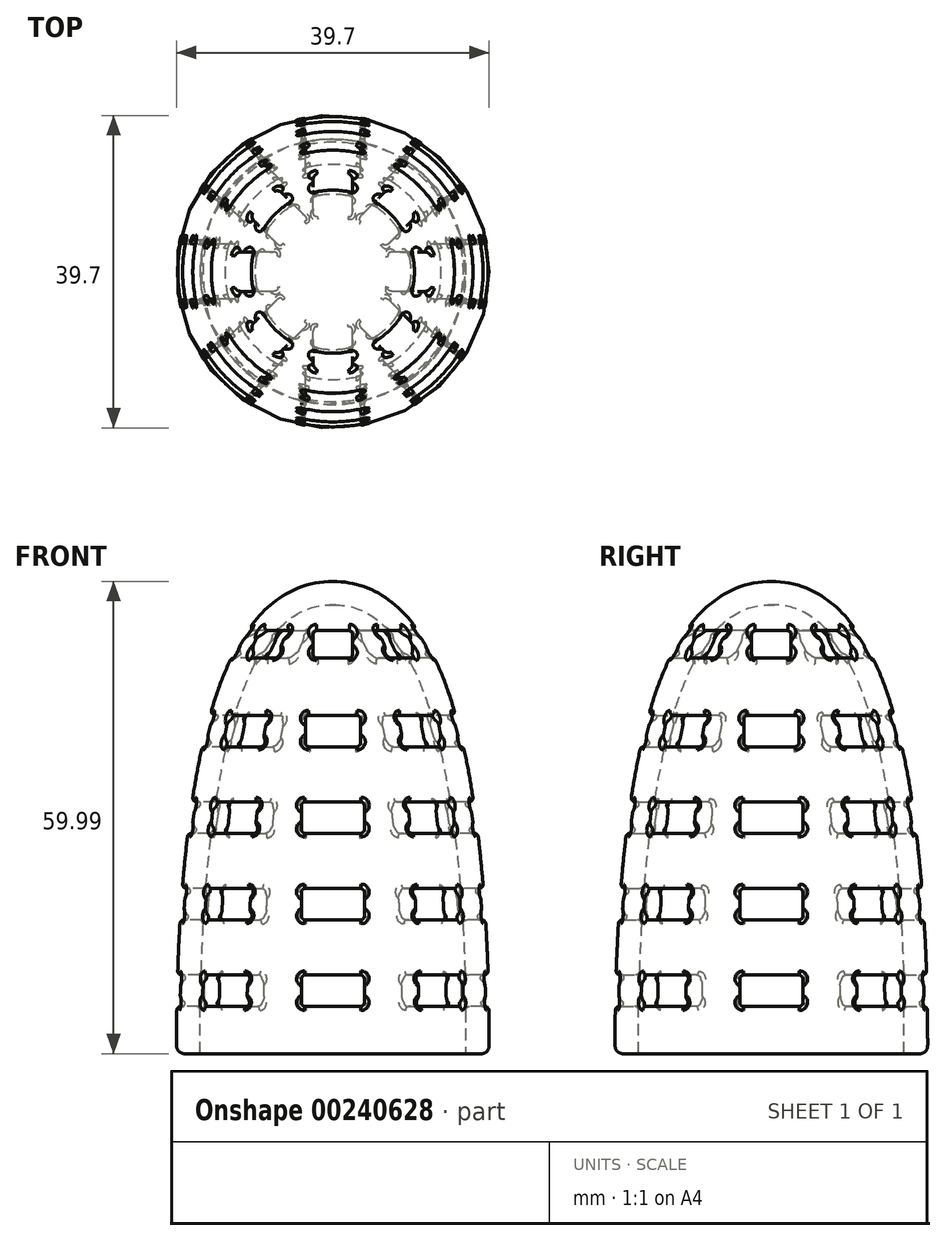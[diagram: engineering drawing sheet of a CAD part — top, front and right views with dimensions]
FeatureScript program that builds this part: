
annotation { "Feature Type Name" : "Feature", "Feature Type Description" : "" }
export const myFeature = defineFeature(function(context is Context, id is Id, definition is map)
    precondition{}
    {
        {
            var Q0;
            Q0=qCreatedBy(makeId("Front.planeOp"),FACE);
            var sketch = newSketch(context, id + "F0", { "sketchPlane" : qUnion([Q0])});
            skFitSpline(sketch, "E0", {"points": [v(0, 60) * mm, v(13.59, 48.77) * mm, v(19.85, 0) * mm], "startDerivative": vector(45.9, 0) * mm, "endDerivative": vector(-0.4, -69.05) * mm});
            skLineSegment(sketch, "E1", {"start": v(19.85, 0) * mm, "end": v(29.85, 0) * mm});
            skFitSpline(sketch, "E2.0", {"points": [v(0, 57) * mm, v(0.73, 57) * mm, v(2.11, 56.84) * mm, v(4.02, 56.13) * mm, v(5.86, 54.92) * mm, v(7.64, 53.14) * mm, v(9.05, 51.12) * mm, v(10.1, 49.2) * mm, v(10.85, 47.59) * mm, v(11.55, 45.81) * mm, v(12.43, 43.25) * mm, v(13.4, 39.7) * mm, v(14.38, 35.02) * mm, v(15.43, 28.37) * mm, v(16.3, 19.58) * mm, v(16.81, 9.16) * mm, v(16.87, 2.86) * mm, v(16.85, 0.02) * mm]});
            skLineSegment(sketch, "E3", {"start": v(16.85, 0.02) * mm, "end": v(11, 0) * mm});
            skLineSegment(sketch, "E4", {"start": v(11, 0) * mm, "end": v(10.99, 4) * mm});
            skLineSegment(sketch, "E5", {"start": v(10.99, 4) * mm, "end": v(16.84, 4.02) * mm});
            skLineSegment(sketch, "E6", {"start": v(16.85, 0.02) * mm, "end": v(19.85, 0) * mm});
            skLineSegment(sketch, "E7", {"start": v(29.85, 0) * mm, "end": v(29.85, 4) * mm});
            skLineSegment(sketch, "E8", {"start": v(29.85, 4) * mm, "end": v(19.84, 4) * mm});
            skLineSegment(sketch, "E9", {"start": v(0, 60) * mm, "end": v(0, 57) * mm});
            skSolve(sketch);
        }
        {
            var Q0;
            Q0=makeQuery(id+"F0.imprint","IMPRINT",FACE,{"disambiguationData":[TD([[makeQuery(id+"F0.imprint","IMPRINT",EDGE,{"derivedFrom":sQuery(id+"F0.wireOp",EDGE,"E0")}),-1.0]])]});
            var Q1;
            Q1=sQuery(id+"F0.wireOp",EDGE,"E9");
            revolve(context, id + "F1", {"entities" : qUnion([Q0]), "axis" : qUnion([Q1]), "revolveType" : RevolveType.FULL});
        }
        {
            var Q0;
            Q0=qCreatedBy(makeId("Front.planeOp"),FACE);
            var sketch = newSketch(context, id + "F2", { "sketchPlane" : qUnion([Q0])});
            skLineSegment(sketch, "E10.bottom", {"start": v(-2.5, 53.75) * mm, "end": v(2.5, 53.75) * mm});
            skLineSegment(sketch, "E10.top", {"start": v(-2.5, 50.25) * mm, "end": v(2.5, 50.25) * mm});
            skLineSegment(sketch, "E10.left", {"start": v(-2.5, 53.75) * mm, "end": v(-2.5, 50.25) * mm});
            skLineSegment(sketch, "E10.right", {"start": v(2.5, 53.75) * mm, "end": v(2.5, 50.25) * mm});
            skPoint(sketch, "E10.middle", {"position": v(0, 52) * mm});
            skLineSegment(sketch, "E11.bottom", {"start": v(-3.5, 43) * mm, "end": v(3.5, 43) * mm});
            skLineSegment(sketch, "E11.top", {"start": v(-3.5, 39) * mm, "end": v(3.5, 39) * mm});
            skLineSegment(sketch, "E11.left", {"start": v(-3.5, 43) * mm, "end": v(-3.5, 39) * mm});
            skLineSegment(sketch, "E11.right", {"start": v(3.5, 43) * mm, "end": v(3.5, 39) * mm});
            skPoint(sketch, "E11.middle", {"position": v(0, 41) * mm});
            skLineSegment(sketch, "E12.bottom", {"start": v(-4, 32) * mm, "end": v(4, 32) * mm});
            skLineSegment(sketch, "E12.top", {"start": v(-4, 28) * mm, "end": v(4, 28) * mm});
            skLineSegment(sketch, "E12.left", {"start": v(-4, 32) * mm, "end": v(-4, 28) * mm});
            skLineSegment(sketch, "E12.right", {"start": v(4, 32) * mm, "end": v(4, 28) * mm});
            skPoint(sketch, "E12.middle", {"position": v(0, 30) * mm});
            skLineSegment(sketch, "E13.bottom", {"start": v(-4, 21) * mm, "end": v(4, 21) * mm});
            skLineSegment(sketch, "E13.top", {"start": v(-4, 17) * mm, "end": v(4, 17) * mm});
            skLineSegment(sketch, "E13.left", {"start": v(-4, 21) * mm, "end": v(-4, 17) * mm});
            skLineSegment(sketch, "E13.right", {"start": v(4, 21) * mm, "end": v(4, 17) * mm});
            skPoint(sketch, "E13.middle", {"position": v(0, 19) * mm});
            skLineSegment(sketch, "E14.bottom", {"start": v(-4, 10) * mm, "end": v(4, 10) * mm});
            skLineSegment(sketch, "E14.top", {"start": v(-4, 6) * mm, "end": v(4, 6) * mm});
            skLineSegment(sketch, "E14.left", {"start": v(-4, 10) * mm, "end": v(-4, 6) * mm});
            skLineSegment(sketch, "E14.right", {"start": v(4, 10) * mm, "end": v(4, 6) * mm});
            skPoint(sketch, "E14.middle", {"position": v(0, 8) * mm});
            skSolve(sketch);
        }
        {
            var Q0;
            Q0 = qSketchRegion(id + "F2", true);
            extrude(context, id + "F3", {"entities" : qUnion([Q0]), "operationType" : NewBodyOperationType.REMOVE, "endBound" : BoundingType.SYMMETRIC, "depth" : 50 * mm});
        }
        {
            var Q0;
            Q0=makeQuery(id+"F3.boolean.opBoolean","COPY",EDGE,{"disambiguationData":[OD(0.0)],"derivedFrom":makeQuery(id+"F3.opExtrude","SWEPT_EDGE",EDGE,{"disambiguationData":[OSD([sQuery(id+"F2.wireOp",EDGE,"E11.top"),sQuery(id+"F2.wireOp",EDGE,"E11.left")])]})});
            var Q1;
            Q1=makeQuery(id+"F3.boolean.opBoolean","COPY",EDGE,{"disambiguationData":[OD(0.0)],"derivedFrom":makeQuery(id+"F3.opExtrude","SWEPT_EDGE",EDGE,{"disambiguationData":[OSD([sQuery(id+"F2.wireOp",EDGE,"E11.top"),sQuery(id+"F2.wireOp",EDGE,"E11.right")])]})});
            var Q2;
            Q2=makeQuery(id+"F3.boolean.opBoolean","COPY",EDGE,{"disambiguationData":[OD(0.0)],"derivedFrom":makeQuery(id+"F3.opExtrude","SWEPT_EDGE",EDGE,{"disambiguationData":[OSD([sQuery(id+"F2.wireOp",EDGE,"E11.bottom"),sQuery(id+"F2.wireOp",EDGE,"E11.left")])]})});
            var Q3;
            Q3=makeQuery(id+"F3.boolean.opBoolean","COPY",EDGE,{"disambiguationData":[OD(0.0)],"derivedFrom":makeQuery(id+"F3.opExtrude","SWEPT_EDGE",EDGE,{"disambiguationData":[OSD([sQuery(id+"F2.wireOp",EDGE,"E10.bottom"),sQuery(id+"F2.wireOp",EDGE,"E10.left")])]})});
            var Q4;
            Q4=makeQuery(id+"F3.boolean.opBoolean","COPY",EDGE,{"disambiguationData":[OD(1.0)],"derivedFrom":makeQuery(id+"F3.opExtrude","SWEPT_EDGE",EDGE,{"disambiguationData":[OSD([sQuery(id+"F2.wireOp",EDGE,"E11.bottom"),sQuery(id+"F2.wireOp",EDGE,"E11.right")])]})});
            var Q5;
            Q5=makeQuery(id+"F3.boolean.opBoolean","COPY",EDGE,{"disambiguationData":[OD(1.0)],"derivedFrom":makeQuery(id+"F3.opExtrude","SWEPT_EDGE",EDGE,{"disambiguationData":[OSD([sQuery(id+"F2.wireOp",EDGE,"E10.bottom"),sQuery(id+"F2.wireOp",EDGE,"E10.right")])]})});
            var Q6;
            Q6=makeQuery(id+"F3.boolean.opBoolean","COPY",EDGE,{"disambiguationData":[OD(0.0)],"derivedFrom":makeQuery(id+"F3.opExtrude","SWEPT_EDGE",EDGE,{"disambiguationData":[OSD([sQuery(id+"F2.wireOp",EDGE,"E10.bottom"),sQuery(id+"F2.wireOp",EDGE,"E10.right")])]})});
            var Q7;
            Q7=makeQuery(id+"F3.boolean.opBoolean","COPY",EDGE,{"disambiguationData":[OD(0.0)],"derivedFrom":makeQuery(id+"F3.opExtrude","SWEPT_EDGE",EDGE,{"disambiguationData":[OSD([sQuery(id+"F2.wireOp",EDGE,"E11.bottom"),sQuery(id+"F2.wireOp",EDGE,"E11.right")])]})});
            var Q8;
            Q8=makeQuery(id+"F3.boolean.opBoolean","COPY",EDGE,{"disambiguationData":[OD(0.0)],"derivedFrom":makeQuery(id+"F3.opExtrude","SWEPT_EDGE",EDGE,{"disambiguationData":[OSD([sQuery(id+"F2.wireOp",EDGE,"E13.top"),sQuery(id+"F2.wireOp",EDGE,"E13.left")])]})});
            var Q9;
            Q9=makeQuery(id+"F3.boolean.opBoolean","COPY",EDGE,{"disambiguationData":[OD(0.0)],"derivedFrom":makeQuery(id+"F3.opExtrude","SWEPT_EDGE",EDGE,{"disambiguationData":[OSD([sQuery(id+"F2.wireOp",EDGE,"E14.top"),sQuery(id+"F2.wireOp",EDGE,"E14.left")])]})});
            var Q10;
            Q10=makeQuery(id+"F3.boolean.opBoolean","COPY",FACE,{"disambiguationData":[OD(0.0)],"derivedFrom":makeQuery(id+"F3.opExtrude","SWEPT_FACE",FACE,{"disambiguationData":[OSD([sQuery(id+"F2.wireOp",EDGE,"E14.top")])]})});
            var Q11;
            Q11=makeQuery(id+"F3.boolean.opBoolean","COPY",FACE,{"disambiguationData":[OD(0.0)],"derivedFrom":makeQuery(id+"F3.opExtrude","SWEPT_FACE",FACE,{"disambiguationData":[OSD([sQuery(id+"F2.wireOp",EDGE,"E14.bottom")])]})});
            var Q12;
            Q12=makeQuery(id+"F3.boolean.opBoolean","COPY",FACE,{"disambiguationData":[OD(0.0)],"derivedFrom":makeQuery(id+"F3.opExtrude","SWEPT_FACE",FACE,{"disambiguationData":[OSD([sQuery(id+"F2.wireOp",EDGE,"E13.bottom")])]})});
            var Q13;
            Q13=makeQuery(id+"F3.boolean.opBoolean","COPY",FACE,{"disambiguationData":[OD(0.0)],"derivedFrom":makeQuery(id+"F3.opExtrude","SWEPT_FACE",FACE,{"disambiguationData":[OSD([sQuery(id+"F2.wireOp",EDGE,"E12.top")])]})});
            var Q14;
            Q14=makeQuery(id+"F3.boolean.opBoolean","COPY",FACE,{"disambiguationData":[OD(0.0)],"derivedFrom":makeQuery(id+"F3.opExtrude","SWEPT_FACE",FACE,{"disambiguationData":[OSD([sQuery(id+"F2.wireOp",EDGE,"E13.top")])]})});
            var Q15;
            Q15=makeQuery(id+"F3.boolean.opBoolean","INTERSECT",EDGE,{"disambiguationData":[OD(0.0)],"derivedFrom":[makeQuery(id+"F1.opRevolve","SWEPT_FACE",FACE,{"disambiguationData":[OSD([sQuery(id+"F0.wireOp",EDGE,"E0")])]}),makeQuery(id+"F3.opExtrude","SWEPT_FACE",FACE,{"disambiguationData":[OSD([sQuery(id+"F2.wireOp",EDGE,"E12.bottom")])]})]});
            var Q16;
            Q16=makeQuery(id+"F3.boolean.opBoolean","COPY",FACE,{"disambiguationData":[OD(0.0)],"derivedFrom":makeQuery(id+"F3.opExtrude","SWEPT_FACE",FACE,{"disambiguationData":[OSD([sQuery(id+"F2.wireOp",EDGE,"E12.bottom")])]})});
            var Q17;
            Q17=makeQuery(id+"F3.boolean.opBoolean","COPY",FACE,{"disambiguationData":[OD(0.0)],"derivedFrom":makeQuery(id+"F3.opExtrude","SWEPT_FACE",FACE,{"disambiguationData":[OSD([sQuery(id+"F2.wireOp",EDGE,"E11.bottom")])]})});
            var Q18;
            Q18=makeQuery(id+"F3.boolean.opBoolean","COPY",FACE,{"disambiguationData":[OD(0.0)],"derivedFrom":makeQuery(id+"F3.opExtrude","SWEPT_FACE",FACE,{"disambiguationData":[OSD([sQuery(id+"F2.wireOp",EDGE,"E11.top")])]})});
            var Q19;
            Q19=makeQuery(id+"F3.boolean.opBoolean","COPY",FACE,{"disambiguationData":[OD(0.0)],"derivedFrom":makeQuery(id+"F3.opExtrude","SWEPT_FACE",FACE,{"disambiguationData":[OSD([sQuery(id+"F2.wireOp",EDGE,"E10.top")])]})});
            var Q20;
            Q20=makeQuery(id+"F3.boolean.opBoolean","COPY",FACE,{"disambiguationData":[OD(0.0)],"derivedFrom":makeQuery(id+"F3.opExtrude","SWEPT_FACE",FACE,{"disambiguationData":[OSD([sQuery(id+"F2.wireOp",EDGE,"E10.bottom")])]})});
            var Q21;
            Q21=makeQuery(id+"F3.boolean.opBoolean","COPY",FACE,{"disambiguationData":[OD(1.0)],"derivedFrom":makeQuery(id+"F3.opExtrude","SWEPT_FACE",FACE,{"disambiguationData":[OSD([sQuery(id+"F2.wireOp",EDGE,"E11.bottom")])]})});
            var Q22;
            Q22=makeQuery(id+"F3.boolean.opBoolean","COPY",FACE,{"disambiguationData":[OD(1.0)],"derivedFrom":makeQuery(id+"F3.opExtrude","SWEPT_FACE",FACE,{"disambiguationData":[OSD([sQuery(id+"F2.wireOp",EDGE,"E12.bottom")])]})});
            var Q23;
            Q23=makeQuery(id+"F3.boolean.opBoolean","COPY",FACE,{"disambiguationData":[OD(1.0)],"derivedFrom":makeQuery(id+"F3.opExtrude","SWEPT_FACE",FACE,{"disambiguationData":[OSD([sQuery(id+"F2.wireOp",EDGE,"E13.bottom")])]})});
            var Q24;
            Q24=makeQuery(id+"F3.boolean.opBoolean","COPY",FACE,{"disambiguationData":[OD(1.0)],"derivedFrom":makeQuery(id+"F3.opExtrude","SWEPT_FACE",FACE,{"disambiguationData":[OSD([sQuery(id+"F2.wireOp",EDGE,"E10.bottom")])]})});
            var Q25;
            Q25=makeQuery(id+"F3.boolean.opBoolean","COPY",FACE,{"disambiguationData":[OD(1.0)],"derivedFrom":makeQuery(id+"F3.opExtrude","SWEPT_FACE",FACE,{"disambiguationData":[OSD([sQuery(id+"F2.wireOp",EDGE,"E14.top")])]})});
            var Q26;
            Q26=makeQuery(id+"F3.boolean.opBoolean","COPY",FACE,{"disambiguationData":[OD(1.0)],"derivedFrom":makeQuery(id+"F3.opExtrude","SWEPT_FACE",FACE,{"disambiguationData":[OSD([sQuery(id+"F2.wireOp",EDGE,"E13.top")])]})});
            var Q27;
            Q27=makeQuery(id+"F3.boolean.opBoolean","COPY",FACE,{"disambiguationData":[OD(1.0)],"derivedFrom":makeQuery(id+"F3.opExtrude","SWEPT_FACE",FACE,{"disambiguationData":[OSD([sQuery(id+"F2.wireOp",EDGE,"E12.top")])]})});
            var Q28;
            Q28=makeQuery(id+"F3.boolean.opBoolean","COPY",FACE,{"disambiguationData":[OD(1.0)],"derivedFrom":makeQuery(id+"F3.opExtrude","SWEPT_FACE",FACE,{"disambiguationData":[OSD([sQuery(id+"F2.wireOp",EDGE,"E11.top")])]})});
            var Q29;
            Q29=makeQuery(id+"F3.boolean.opBoolean","COPY",FACE,{"disambiguationData":[OD(1.0)],"derivedFrom":makeQuery(id+"F3.opExtrude","SWEPT_FACE",FACE,{"disambiguationData":[OSD([sQuery(id+"F2.wireOp",EDGE,"E10.top")])]})});
            var Q30;
            Q30=makeQuery(id+"F3.boolean.opBoolean","COPY",FACE,{"disambiguationData":[OD(1.0)],"derivedFrom":makeQuery(id+"F3.opExtrude","SWEPT_FACE",FACE,{"disambiguationData":[OSD([sQuery(id+"F2.wireOp",EDGE,"E14.bottom")])]})});
            fillet(context, id + "F4", {"entities" : qUnion([Q0, Q1, Q2, Q3, Q4, Q5, Q6, Q7, Q8, Q9, Q10, Q11, Q12, Q13, Q14, Q15, Q16, Q17, Q18, Q19, Q20, Q21, Q22, Q23, Q24, Q25, Q26, Q27, Q28, Q29, Q30]), "radius" : .5 * mm, "tangentPropagation" : true, "allowEdgeOverflow" : false});
        }
        {
            var Q0;
            Q0=qCreatedBy(makeId("Right.planeOp"),FACE);
            var sketch = newSketch(context, id + "F5", { "sketchPlane" : qUnion([Q0])});
            skLineSegment(sketch, "E15.bottom", {"start": v(2.5, 53.75) * mm, "end": v(-2.5, 53.75) * mm});
            skLineSegment(sketch, "E15.top", {"start": v(2.5, 50.25) * mm, "end": v(-2.5, 50.25) * mm});
            skLineSegment(sketch, "E15.left", {"start": v(2.5, 53.75) * mm, "end": v(2.5, 50.25) * mm});
            skLineSegment(sketch, "E15.right", {"start": v(-2.5, 53.75) * mm, "end": v(-2.5, 50.25) * mm});
            skPoint(sketch, "E15.middle", {"position": v(0, 52) * mm});
            skLineSegment(sketch, "E16.bottom", {"start": v(3.5, 43) * mm, "end": v(-3.5, 43) * mm});
            skLineSegment(sketch, "E16.top", {"start": v(3.5, 39) * mm, "end": v(-3.5, 39) * mm});
            skLineSegment(sketch, "E16.left", {"start": v(3.5, 43) * mm, "end": v(3.5, 39) * mm});
            skLineSegment(sketch, "E16.right", {"start": v(-3.5, 43) * mm, "end": v(-3.5, 39) * mm});
            skPoint(sketch, "E16.middle", {"position": v(0, 41) * mm});
            skLineSegment(sketch, "E17.bottom", {"start": v(4, 32) * mm, "end": v(-4, 32) * mm});
            skLineSegment(sketch, "E17.top", {"start": v(4, 28) * mm, "end": v(-4, 28) * mm});
            skLineSegment(sketch, "E17.left", {"start": v(4, 32) * mm, "end": v(4, 28) * mm});
            skLineSegment(sketch, "E17.right", {"start": v(-4, 32) * mm, "end": v(-4, 28) * mm});
            skPoint(sketch, "E17.middle", {"position": v(0, 30) * mm});
            skLineSegment(sketch, "E18.bottom", {"start": v(4, 21) * mm, "end": v(-4, 21) * mm});
            skLineSegment(sketch, "E18.top", {"start": v(4, 17) * mm, "end": v(-4, 17) * mm});
            skLineSegment(sketch, "E18.left", {"start": v(4, 21) * mm, "end": v(4, 17) * mm});
            skLineSegment(sketch, "E18.right", {"start": v(-4, 21) * mm, "end": v(-4, 17) * mm});
            skPoint(sketch, "E18.middle", {"position": v(0, 19) * mm});
            skLineSegment(sketch, "E19.bottom", {"start": v(4, 10) * mm, "end": v(-4, 10) * mm});
            skLineSegment(sketch, "E19.top", {"start": v(4, 6) * mm, "end": v(-4, 6) * mm});
            skLineSegment(sketch, "E19.left", {"start": v(4, 10) * mm, "end": v(4, 6) * mm});
            skLineSegment(sketch, "E19.right", {"start": v(-4, 10) * mm, "end": v(-4, 6) * mm});
            skPoint(sketch, "E19.middle", {"position": v(0, 8) * mm});
            skSolve(sketch);
        }
        {
            var Q0;
            Q0 = qSketchRegion(id + "F5", true);
            extrude(context, id + "F6", {"entities" : qUnion([Q0]), "operationType" : NewBodyOperationType.REMOVE, "endBound" : BoundingType.SYMMETRIC, "depth" : 50 * mm});
        }
        {
            var Q0;
            Q0=qCreatedBy(makeId("Front.planeOp"),FACE);
            var Q1;
            Q1=sQuery(id+"F0.wireOp",EDGE,"E7");
            cPlane(context, id + "F7", {"entities" : qUnion([Q0, Q1]), "cplaneType" : CPlaneType.LINE_ANGLE, "offset" : 25 * mm, "angle" : 45 * degree, "width" : 150 * mm, "height" : 150 * mm});
        }
        {
            var Q0;
            Q0=qCreatedBy(id+"F7.planeOp",FACE);
            var sketch = newSketch(context, id + "F8", { "sketchPlane" : qUnion([Q0])});
            skLineSegment(sketch, "E20.bottom", {"start": v(3.5, 43) * mm, "end": v(-3.5, 43) * mm});
            skLineSegment(sketch, "E20.top", {"start": v(3.5, 39) * mm, "end": v(-3.5, 39) * mm});
            skLineSegment(sketch, "E20.left", {"start": v(3.5, 43) * mm, "end": v(3.5, 39) * mm});
            skLineSegment(sketch, "E20.right", {"start": v(-3.5, 43) * mm, "end": v(-3.5, 39) * mm});
            skPoint(sketch, "E20.middle", {"position": v(0, 41) * mm});
            skLineSegment(sketch, "E21.bottom", {"start": v(4, 32) * mm, "end": v(-4, 32) * mm});
            skLineSegment(sketch, "E21.top", {"start": v(4, 28) * mm, "end": v(-4, 28) * mm});
            skLineSegment(sketch, "E21.left", {"start": v(4, 32) * mm, "end": v(4, 28) * mm});
            skLineSegment(sketch, "E21.right", {"start": v(-4, 32) * mm, "end": v(-4, 28) * mm});
            skPoint(sketch, "E21.middle", {"position": v(0, 30) * mm});
            skLineSegment(sketch, "E22.bottom", {"start": v(4, 21) * mm, "end": v(-4, 21) * mm});
            skLineSegment(sketch, "E22.top", {"start": v(4, 17) * mm, "end": v(-4, 17) * mm});
            skLineSegment(sketch, "E22.left", {"start": v(4, 21) * mm, "end": v(4, 17) * mm});
            skLineSegment(sketch, "E22.right", {"start": v(-4, 21) * mm, "end": v(-4, 17) * mm});
            skPoint(sketch, "E22.middle", {"position": v(0, 19) * mm});
            skLineSegment(sketch, "E23.bottom", {"start": v(4, 10) * mm, "end": v(-4, 10) * mm});
            skLineSegment(sketch, "E23.top", {"start": v(4, 6) * mm, "end": v(-4, 6) * mm});
            skLineSegment(sketch, "E23.left", {"start": v(4, 10) * mm, "end": v(4, 6) * mm});
            skLineSegment(sketch, "E23.right", {"start": v(-4, 10) * mm, "end": v(-4, 6) * mm});
            skPoint(sketch, "E23.middle", {"position": v(0, 8) * mm});
            skLineSegment(sketch, "E24.bottom", {"start": v(2.5, 53.75) * mm, "end": v(-2.5, 53.75) * mm});
            skLineSegment(sketch, "E24.top", {"start": v(2.5, 50.25) * mm, "end": v(-2.5, 50.25) * mm});
            skLineSegment(sketch, "E24.left", {"start": v(2.5, 53.75) * mm, "end": v(2.5, 50.25) * mm});
            skLineSegment(sketch, "E24.right", {"start": v(-2.5, 53.75) * mm, "end": v(-2.5, 50.25) * mm});
            skPoint(sketch, "E24.middle", {"position": v(0, 52) * mm});
            skSolve(sketch);
        }
        {
            var Q0;
            Q0 = qSketchRegion(id + "F8", true);
            extrude(context, id + "F9", {"entities" : qUnion([Q0]), "operationType" : NewBodyOperationType.REMOVE, "depth" : 50 * mm});
        }
        {
            var Q0;
            Q0=qCreatedBy(makeId("Right.planeOp"),FACE);
            var Q1;
            Q1=sQuery(id+"F0.wireOp",EDGE,"E7");
            cPlane(context, id + "F10", {"entities" : qUnion([Q0, Q1]), "cplaneType" : CPlaneType.LINE_ANGLE, "offset" : 25 * mm, "angle" : 45 * degree, "width" : 150 * mm, "height" : 150 * mm});
        }
        {
            var Q0;
            Q0=qCreatedBy(id+"F10.planeOp",FACE);
            var sketch = newSketch(context, id + "F11", { "sketchPlane" : qUnion([Q0])});
            skLineSegment(sketch, "E25.bottom", {"start": v(-2.5, 53.75) * mm, "end": v(2.5, 53.75) * mm});
            skLineSegment(sketch, "E25.top", {"start": v(-2.5, 50.25) * mm, "end": v(2.5, 50.25) * mm});
            skLineSegment(sketch, "E25.left", {"start": v(-2.5, 53.75) * mm, "end": v(-2.5, 50.25) * mm});
            skLineSegment(sketch, "E25.right", {"start": v(2.5, 53.75) * mm, "end": v(2.5, 50.25) * mm});
            skPoint(sketch, "E25.middle", {"position": v(0, 52) * mm});
            skLineSegment(sketch, "E26.bottom", {"start": v(-3.5, 43) * mm, "end": v(3.5, 43) * mm});
            skLineSegment(sketch, "E26.top", {"start": v(-3.5, 39) * mm, "end": v(3.5, 39) * mm});
            skLineSegment(sketch, "E26.left", {"start": v(-3.5, 43) * mm, "end": v(-3.5, 39) * mm});
            skLineSegment(sketch, "E26.right", {"start": v(3.5, 43) * mm, "end": v(3.5, 39) * mm});
            skPoint(sketch, "E26.middle", {"position": v(0, 41) * mm});
            skLineSegment(sketch, "E27.bottom", {"start": v(-4, 32) * mm, "end": v(4, 32) * mm});
            skLineSegment(sketch, "E27.top", {"start": v(-4, 28) * mm, "end": v(4, 28) * mm});
            skLineSegment(sketch, "E27.left", {"start": v(-4, 32) * mm, "end": v(-4, 28) * mm});
            skLineSegment(sketch, "E27.right", {"start": v(4, 32) * mm, "end": v(4, 28) * mm});
            skPoint(sketch, "E27.middle", {"position": v(0, 30) * mm});
            skLineSegment(sketch, "E28.bottom", {"start": v(-4, 21) * mm, "end": v(4, 21) * mm});
            skLineSegment(sketch, "E28.top", {"start": v(-4, 17) * mm, "end": v(4, 17) * mm});
            skLineSegment(sketch, "E28.left", {"start": v(-4, 21) * mm, "end": v(-4, 17) * mm});
            skLineSegment(sketch, "E28.right", {"start": v(4, 21) * mm, "end": v(4, 17) * mm});
            skPoint(sketch, "E28.middle", {"position": v(0, 19) * mm});
            skLineSegment(sketch, "E29.bottom", {"start": v(-4, 10) * mm, "end": v(4, 10) * mm});
            skLineSegment(sketch, "E29.top", {"start": v(-4, 6) * mm, "end": v(4, 6) * mm});
            skLineSegment(sketch, "E29.left", {"start": v(-4, 10) * mm, "end": v(-4, 6) * mm});
            skLineSegment(sketch, "E29.right", {"start": v(4, 10) * mm, "end": v(4, 6) * mm});
            skPoint(sketch, "E29.middle", {"position": v(0, 8) * mm});
            skSolve(sketch);
        }
        {
            var Q0;
            Q0 = qSketchRegion(id + "F11", true);
            extrude(context, id + "F12", {"entities" : qUnion([Q0]), "operationType" : NewBodyOperationType.REMOVE, "depth" : 50 * mm});
        }
        {
            var Q0;
            Q0=makeQuery(id+"F9.boolean.opBoolean","COPY",FACE,{"disambiguationData":[OD(0.0)],"derivedFrom":makeQuery(id+"F9.opExtrude","SWEPT_FACE",FACE,{"disambiguationData":[OSD([sQuery(id+"F8.wireOp",EDGE,"E20.bottom")])]})});
            var Q1;
            Q1=makeQuery(id+"F9.boolean.opBoolean","COPY",FACE,{"disambiguationData":[OD(0.0)],"derivedFrom":makeQuery(id+"F9.opExtrude","SWEPT_FACE",FACE,{"disambiguationData":[OSD([sQuery(id+"F8.wireOp",EDGE,"E21.bottom")])]})});
            var Q2;
            Q2=makeQuery(id+"F6.boolean.opBoolean","COPY",FACE,{"disambiguationData":[OD(0.0)],"derivedFrom":makeQuery(id+"F6.opExtrude","SWEPT_FACE",FACE,{"disambiguationData":[OSD([sQuery(id+"F5.wireOp",EDGE,"E16.bottom")])]})});
            var Q3;
            Q3=makeQuery(id+"F6.boolean.opBoolean","COPY",FACE,{"disambiguationData":[OD(0.0)],"derivedFrom":makeQuery(id+"F6.opExtrude","SWEPT_FACE",FACE,{"disambiguationData":[OSD([sQuery(id+"F5.wireOp",EDGE,"E17.bottom")])]})});
            var Q4;
            Q4=makeQuery(id+"F6.boolean.opBoolean","COPY",FACE,{"disambiguationData":[OD(0.0)],"derivedFrom":makeQuery(id+"F6.opExtrude","SWEPT_FACE",FACE,{"disambiguationData":[OSD([sQuery(id+"F5.wireOp",EDGE,"E18.bottom")])]})});
            var Q5;
            Q5=makeQuery(id+"F9.boolean.opBoolean","COPY",FACE,{"disambiguationData":[OD(0.0)],"derivedFrom":makeQuery(id+"F9.opExtrude","SWEPT_FACE",FACE,{"disambiguationData":[OSD([sQuery(id+"F8.wireOp",EDGE,"E22.bottom")])]})});
            var Q6;
            Q6=makeQuery(id+"F6.boolean.opBoolean","COPY",FACE,{"disambiguationData":[OD(0.0)],"derivedFrom":makeQuery(id+"F6.opExtrude","SWEPT_FACE",FACE,{"disambiguationData":[OSD([sQuery(id+"F5.wireOp",EDGE,"E15.bottom")])]})});
            var Q7;
            Q7=makeQuery(id+"F9.boolean.opBoolean","COPY",FACE,{"disambiguationData":[OD(0.0)],"derivedFrom":makeQuery(id+"F9.opExtrude","SWEPT_FACE",FACE,{"disambiguationData":[OSD([sQuery(id+"F8.wireOp",EDGE,"E24.bottom")])]})});
            var Q8;
            Q8=makeQuery(id+"F12.boolean.opBoolean","COPY",FACE,{"disambiguationData":[OD(0.0)],"derivedFrom":makeQuery(id+"F12.opExtrude","SWEPT_FACE",FACE,{"disambiguationData":[OSD([sQuery(id+"F11.wireOp",EDGE,"E26.bottom")])]})});
            var Q9;
            Q9=makeQuery(id+"F12.boolean.opBoolean","INTERSECT",EDGE,{"disambiguationData":[OD(0.0)],"derivedFrom":[makeQuery(id+"F1.opRevolve","SWEPT_FACE",FACE,{"disambiguationData":[OSD([sQuery(id+"F0.wireOp",EDGE,"E0")])]}),makeQuery(id+"F12.opExtrude","SWEPT_FACE",FACE,{"disambiguationData":[OSD([sQuery(id+"F11.wireOp",EDGE,"E27.bottom")])]})]});
            var Q10;
            Q10=makeQuery(id+"F12.boolean.opBoolean","COPY",FACE,{"disambiguationData":[OD(0.0)],"derivedFrom":makeQuery(id+"F12.opExtrude","SWEPT_FACE",FACE,{"disambiguationData":[OSD([sQuery(id+"F11.wireOp",EDGE,"E27.bottom")])]})});
            var Q11;
            Q11=makeQuery(id+"F12.boolean.opBoolean","COPY",FACE,{"disambiguationData":[OD(0.0)],"derivedFrom":makeQuery(id+"F12.opExtrude","SWEPT_FACE",FACE,{"disambiguationData":[OSD([sQuery(id+"F11.wireOp",EDGE,"E28.bottom")])]})});
            var Q12;
            Q12=makeQuery(id+"F6.boolean.opBoolean","COPY",FACE,{"disambiguationData":[OD(0.0)],"derivedFrom":makeQuery(id+"F6.opExtrude","SWEPT_FACE",FACE,{"disambiguationData":[OSD([sQuery(id+"F5.wireOp",EDGE,"E19.top")])]})});
            var Q13;
            Q13=makeQuery(id+"F9.boolean.opBoolean","COPY",FACE,{"disambiguationData":[OD(0.0)],"derivedFrom":makeQuery(id+"F9.opExtrude","SWEPT_FACE",FACE,{"disambiguationData":[OSD([sQuery(id+"F8.wireOp",EDGE,"E23.top")])]})});
            var Q14;
            Q14=makeQuery(id+"F9.boolean.opBoolean","COPY",FACE,{"disambiguationData":[OD(0.0)],"derivedFrom":makeQuery(id+"F9.opExtrude","SWEPT_FACE",FACE,{"disambiguationData":[OSD([sQuery(id+"F8.wireOp",EDGE,"E22.top")])]})});
            var Q15;
            Q15=makeQuery(id+"F9.boolean.opBoolean","COPY",FACE,{"disambiguationData":[OD(0.0)],"derivedFrom":makeQuery(id+"F9.opExtrude","SWEPT_FACE",FACE,{"disambiguationData":[OSD([sQuery(id+"F8.wireOp",EDGE,"E21.top")])]})});
            var Q16;
            Q16=makeQuery(id+"F9.boolean.opBoolean","COPY",FACE,{"disambiguationData":[OD(0.0)],"derivedFrom":makeQuery(id+"F9.opExtrude","SWEPT_FACE",FACE,{"disambiguationData":[OSD([sQuery(id+"F8.wireOp",EDGE,"E20.top")])]})});
            var Q17;
            Q17=makeQuery(id+"F6.boolean.opBoolean","COPY",FACE,{"disambiguationData":[OD(0.0)],"derivedFrom":makeQuery(id+"F6.opExtrude","SWEPT_FACE",FACE,{"disambiguationData":[OSD([sQuery(id+"F5.wireOp",EDGE,"E17.top")])]})});
            var Q18;
            Q18=makeQuery(id+"F6.boolean.opBoolean","COPY",FACE,{"disambiguationData":[OD(0.0)],"derivedFrom":makeQuery(id+"F6.opExtrude","SWEPT_FACE",FACE,{"disambiguationData":[OSD([sQuery(id+"F5.wireOp",EDGE,"E16.top")])]})});
            var Q19;
            Q19=makeQuery(id+"F6.boolean.opBoolean","COPY",FACE,{"disambiguationData":[OD(0.0)],"derivedFrom":makeQuery(id+"F6.opExtrude","SWEPT_FACE",FACE,{"disambiguationData":[OSD([sQuery(id+"F5.wireOp",EDGE,"E15.top")])]})});
            var Q20;
            Q20=makeQuery(id+"F9.boolean.opBoolean","COPY",FACE,{"disambiguationData":[OD(0.0)],"derivedFrom":makeQuery(id+"F9.opExtrude","SWEPT_FACE",FACE,{"disambiguationData":[OSD([sQuery(id+"F8.wireOp",EDGE,"E24.top")])]})});
            var Q21;
            Q21=makeQuery(id+"F12.boolean.opBoolean","COPY",FACE,{"disambiguationData":[OD(0.0)],"derivedFrom":makeQuery(id+"F12.opExtrude","SWEPT_FACE",FACE,{"disambiguationData":[OSD([sQuery(id+"F11.wireOp",EDGE,"E25.top")])]})});
            var Q22;
            Q22=makeQuery(id+"F12.boolean.opBoolean","COPY",FACE,{"disambiguationData":[OD(0.0)],"derivedFrom":makeQuery(id+"F12.opExtrude","SWEPT_FACE",FACE,{"disambiguationData":[OSD([sQuery(id+"F11.wireOp",EDGE,"E26.top")])]})});
            var Q23;
            Q23=makeQuery(id+"F12.boolean.opBoolean","COPY",FACE,{"disambiguationData":[OD(0.0)],"derivedFrom":makeQuery(id+"F12.opExtrude","SWEPT_FACE",FACE,{"disambiguationData":[OSD([sQuery(id+"F11.wireOp",EDGE,"E27.top")])]})});
            var Q24;
            Q24=makeQuery(id+"F12.boolean.opBoolean","COPY",FACE,{"disambiguationData":[OD(0.0)],"derivedFrom":makeQuery(id+"F12.opExtrude","SWEPT_FACE",FACE,{"disambiguationData":[OSD([sQuery(id+"F11.wireOp",EDGE,"E28.top")])]})});
            var Q25;
            Q25=makeQuery(id+"F12.boolean.opBoolean","COPY",FACE,{"disambiguationData":[OD(0.0)],"derivedFrom":makeQuery(id+"F12.opExtrude","SWEPT_FACE",FACE,{"disambiguationData":[OSD([sQuery(id+"F11.wireOp",EDGE,"E29.top")])]})});
            var Q26;
            Q26=makeQuery(id+"F6.boolean.opBoolean","COPY",FACE,{"disambiguationData":[OD(0.0)],"derivedFrom":makeQuery(id+"F6.opExtrude","SWEPT_FACE",FACE,{"disambiguationData":[OSD([sQuery(id+"F5.wireOp",EDGE,"E18.top")])]})});
            var Q27;
            Q27=makeQuery(id+"F6.boolean.opBoolean","COPY",FACE,{"disambiguationData":[OD(0.0)],"derivedFrom":makeQuery(id+"F6.opExtrude","SWEPT_FACE",FACE,{"disambiguationData":[OSD([sQuery(id+"F5.wireOp",EDGE,"E19.bottom")])]})});
            var Q28;
            Q28=makeQuery(id+"F12.boolean.opBoolean","COPY",FACE,{"disambiguationData":[OD(0.0)],"derivedFrom":makeQuery(id+"F12.opExtrude","SWEPT_FACE",FACE,{"disambiguationData":[OSD([sQuery(id+"F11.wireOp",EDGE,"E29.bottom")])]})});
            var Q29;
            Q29=makeQuery(id+"F9.boolean.opBoolean","COPY",FACE,{"disambiguationData":[OD(0.0)],"derivedFrom":makeQuery(id+"F9.opExtrude","SWEPT_FACE",FACE,{"disambiguationData":[OSD([sQuery(id+"F8.wireOp",EDGE,"E23.bottom")])]})});
            var Q30;
            Q30=makeQuery(id+"F12.boolean.opBoolean","COPY",FACE,{"disambiguationData":[OD(0.0)],"derivedFrom":makeQuery(id+"F12.opExtrude","SWEPT_FACE",FACE,{"disambiguationData":[OSD([sQuery(id+"F11.wireOp",EDGE,"E25.bottom")])]})});
            var Q31;
            Q31=makeQuery(id+"F12.boolean.opBoolean","COPY",FACE,{"disambiguationData":[OD(1.0)],"derivedFrom":makeQuery(id+"F12.opExtrude","SWEPT_FACE",FACE,{"disambiguationData":[OSD([sQuery(id+"F11.wireOp",EDGE,"E29.top")])]})});
            var Q32;
            Q32=makeQuery(id+"F6.boolean.opBoolean","COPY",FACE,{"disambiguationData":[OD(1.0)],"derivedFrom":makeQuery(id+"F6.opExtrude","SWEPT_FACE",FACE,{"disambiguationData":[OSD([sQuery(id+"F5.wireOp",EDGE,"E19.top")])]})});
            var Q33;
            Q33=makeQuery(id+"F9.boolean.opBoolean","COPY",FACE,{"disambiguationData":[OD(1.0)],"derivedFrom":makeQuery(id+"F9.opExtrude","SWEPT_FACE",FACE,{"disambiguationData":[OSD([sQuery(id+"F8.wireOp",EDGE,"E23.top")])]})});
            var Q34;
            Q34=makeQuery(id+"F9.boolean.opBoolean","COPY",FACE,{"disambiguationData":[OD(1.0)],"derivedFrom":makeQuery(id+"F9.opExtrude","SWEPT_FACE",FACE,{"disambiguationData":[OSD([sQuery(id+"F8.wireOp",EDGE,"E22.top")])]})});
            var Q35;
            Q35=makeQuery(id+"F6.boolean.opBoolean","COPY",FACE,{"disambiguationData":[OD(1.0)],"derivedFrom":makeQuery(id+"F6.opExtrude","SWEPT_FACE",FACE,{"disambiguationData":[OSD([sQuery(id+"F5.wireOp",EDGE,"E18.top")])]})});
            var Q36;
            Q36=makeQuery(id+"F12.boolean.opBoolean","COPY",FACE,{"disambiguationData":[OD(1.0)],"derivedFrom":makeQuery(id+"F12.opExtrude","SWEPT_FACE",FACE,{"disambiguationData":[OSD([sQuery(id+"F11.wireOp",EDGE,"E28.top")])]})});
            var Q37;
            Q37=makeQuery(id+"F12.boolean.opBoolean","COPY",FACE,{"disambiguationData":[OD(1.0)],"derivedFrom":makeQuery(id+"F12.opExtrude","SWEPT_FACE",FACE,{"disambiguationData":[OSD([sQuery(id+"F11.wireOp",EDGE,"E27.top")])]})});
            var Q38;
            Q38=makeQuery(id+"F6.boolean.opBoolean","COPY",FACE,{"disambiguationData":[OD(1.0)],"derivedFrom":makeQuery(id+"F6.opExtrude","SWEPT_FACE",FACE,{"disambiguationData":[OSD([sQuery(id+"F5.wireOp",EDGE,"E17.top")])]})});
            var Q39;
            Q39=makeQuery(id+"F9.boolean.opBoolean","COPY",FACE,{"disambiguationData":[OD(1.0)],"derivedFrom":makeQuery(id+"F9.opExtrude","SWEPT_FACE",FACE,{"disambiguationData":[OSD([sQuery(id+"F8.wireOp",EDGE,"E21.top")])]})});
            var Q40;
            Q40=makeQuery(id+"F9.boolean.opBoolean","COPY",FACE,{"disambiguationData":[OD(1.0)],"derivedFrom":makeQuery(id+"F9.opExtrude","SWEPT_FACE",FACE,{"disambiguationData":[OSD([sQuery(id+"F8.wireOp",EDGE,"E20.top")])]})});
            var Q41;
            Q41=makeQuery(id+"F6.boolean.opBoolean","COPY",FACE,{"disambiguationData":[OD(1.0)],"derivedFrom":makeQuery(id+"F6.opExtrude","SWEPT_FACE",FACE,{"disambiguationData":[OSD([sQuery(id+"F5.wireOp",EDGE,"E16.top")])]})});
            var Q42;
            Q42=makeQuery(id+"F12.boolean.opBoolean","COPY",FACE,{"disambiguationData":[OD(1.0)],"derivedFrom":makeQuery(id+"F12.opExtrude","SWEPT_FACE",FACE,{"disambiguationData":[OSD([sQuery(id+"F11.wireOp",EDGE,"E26.top")])]})});
            var Q43;
            Q43=makeQuery(id+"F12.boolean.opBoolean","COPY",FACE,{"disambiguationData":[OD(1.0)],"derivedFrom":makeQuery(id+"F12.opExtrude","SWEPT_FACE",FACE,{"disambiguationData":[OSD([sQuery(id+"F11.wireOp",EDGE,"E25.top")])]})});
            var Q44;
            Q44=makeQuery(id+"F6.boolean.opBoolean","COPY",FACE,{"disambiguationData":[OD(1.0)],"derivedFrom":makeQuery(id+"F6.opExtrude","SWEPT_FACE",FACE,{"disambiguationData":[OSD([sQuery(id+"F5.wireOp",EDGE,"E15.top")])]})});
            var Q45;
            Q45=makeQuery(id+"F9.boolean.opBoolean","COPY",FACE,{"disambiguationData":[OD(1.0)],"derivedFrom":makeQuery(id+"F9.opExtrude","SWEPT_FACE",FACE,{"disambiguationData":[OSD([sQuery(id+"F8.wireOp",EDGE,"E24.top")])]})});
            var Q46;
            Q46=makeQuery(id+"F6.boolean.opBoolean","COPY",FACE,{"disambiguationData":[OD(1.0)],"derivedFrom":makeQuery(id+"F6.opExtrude","SWEPT_FACE",FACE,{"disambiguationData":[OSD([sQuery(id+"F5.wireOp",EDGE,"E15.bottom")])]})});
            var Q47;
            Q47=makeQuery(id+"F9.boolean.opBoolean","INTERSECT",EDGE,{"disambiguationData":[OD(1.0)],"derivedFrom":[makeQuery(id+"F1.opRevolve","SWEPT_FACE",FACE,{"disambiguationData":[OSD([sQuery(id+"F0.wireOp",EDGE,"E0")])]}),makeQuery(id+"F9.opExtrude","SWEPT_FACE",FACE,{"disambiguationData":[OSD([sQuery(id+"F8.wireOp",EDGE,"E24.top")])]})]});
            var Q48;
            Q48=makeQuery(id+"F9.boolean.opBoolean","COPY",FACE,{"disambiguationData":[OD(1.0)],"derivedFrom":makeQuery(id+"F9.opExtrude","SWEPT_FACE",FACE,{"disambiguationData":[OSD([sQuery(id+"F8.wireOp",EDGE,"E24.bottom")])]})});
            var Q49;
            Q49=makeQuery(id+"F9.boolean.opBoolean","COPY",FACE,{"disambiguationData":[OD(1.0)],"derivedFrom":makeQuery(id+"F9.opExtrude","SWEPT_FACE",FACE,{"disambiguationData":[OSD([sQuery(id+"F8.wireOp",EDGE,"E20.bottom")])]})});
            var Q50;
            Q50=makeQuery(id+"F6.boolean.opBoolean","COPY",FACE,{"disambiguationData":[OD(1.0)],"derivedFrom":makeQuery(id+"F6.opExtrude","SWEPT_FACE",FACE,{"disambiguationData":[OSD([sQuery(id+"F5.wireOp",EDGE,"E16.bottom")])]})});
            var Q51;
            Q51=makeQuery(id+"F12.boolean.opBoolean","COPY",FACE,{"disambiguationData":[OD(1.0)],"derivedFrom":makeQuery(id+"F12.opExtrude","SWEPT_FACE",FACE,{"disambiguationData":[OSD([sQuery(id+"F11.wireOp",EDGE,"E25.bottom")])]})});
            var Q52;
            Q52=makeQuery(id+"F12.boolean.opBoolean","COPY",FACE,{"disambiguationData":[OD(1.0)],"derivedFrom":makeQuery(id+"F12.opExtrude","SWEPT_FACE",FACE,{"disambiguationData":[OSD([sQuery(id+"F11.wireOp",EDGE,"E26.bottom")])]})});
            var Q53;
            Q53=makeQuery(id+"F12.boolean.opBoolean","COPY",FACE,{"disambiguationData":[OD(1.0)],"derivedFrom":makeQuery(id+"F12.opExtrude","SWEPT_FACE",FACE,{"disambiguationData":[OSD([sQuery(id+"F11.wireOp",EDGE,"E27.bottom")])]})});
            var Q54;
            Q54=makeQuery(id+"F12.boolean.opBoolean","COPY",FACE,{"disambiguationData":[OD(1.0)],"derivedFrom":makeQuery(id+"F12.opExtrude","SWEPT_FACE",FACE,{"disambiguationData":[OSD([sQuery(id+"F11.wireOp",EDGE,"E28.bottom")])]})});
            var Q55;
            Q55=makeQuery(id+"F6.boolean.opBoolean","COPY",FACE,{"disambiguationData":[OD(1.0)],"derivedFrom":makeQuery(id+"F6.opExtrude","SWEPT_FACE",FACE,{"disambiguationData":[OSD([sQuery(id+"F5.wireOp",EDGE,"E18.bottom")])]})});
            var Q56;
            Q56=makeQuery(id+"F6.boolean.opBoolean","COPY",FACE,{"disambiguationData":[OD(1.0)],"derivedFrom":makeQuery(id+"F6.opExtrude","SWEPT_FACE",FACE,{"disambiguationData":[OSD([sQuery(id+"F5.wireOp",EDGE,"E17.bottom")])]})});
            var Q57;
            Q57=makeQuery(id+"F9.boolean.opBoolean","COPY",FACE,{"disambiguationData":[OD(1.0)],"derivedFrom":makeQuery(id+"F9.opExtrude","SWEPT_FACE",FACE,{"disambiguationData":[OSD([sQuery(id+"F8.wireOp",EDGE,"E21.bottom")])]})});
            var Q58;
            Q58=makeQuery(id+"F9.boolean.opBoolean","COPY",FACE,{"disambiguationData":[OD(1.0)],"derivedFrom":makeQuery(id+"F9.opExtrude","SWEPT_FACE",FACE,{"disambiguationData":[OSD([sQuery(id+"F8.wireOp",EDGE,"E22.bottom")])]})});
            var Q59;
            Q59=makeQuery(id+"F6.boolean.opBoolean","COPY",FACE,{"disambiguationData":[OD(1.0)],"derivedFrom":makeQuery(id+"F6.opExtrude","SWEPT_FACE",FACE,{"disambiguationData":[OSD([sQuery(id+"F5.wireOp",EDGE,"E19.bottom")])]})});
            var Q60;
            Q60=makeQuery(id+"F12.boolean.opBoolean","COPY",FACE,{"disambiguationData":[OD(1.0)],"derivedFrom":makeQuery(id+"F12.opExtrude","SWEPT_FACE",FACE,{"disambiguationData":[OSD([sQuery(id+"F11.wireOp",EDGE,"E29.bottom")])]})});
            var Q61;
            Q61=makeQuery(id+"F9.boolean.opBoolean","COPY",FACE,{"disambiguationData":[OD(1.0)],"derivedFrom":makeQuery(id+"F9.opExtrude","SWEPT_FACE",FACE,{"disambiguationData":[OSD([sQuery(id+"F8.wireOp",EDGE,"E23.bottom")])]})});
            fillet(context, id + "F13", {"entities" : qUnion([Q0, Q1, Q2, Q3, Q4, Q5, Q6, Q7, Q8, Q9, Q10, Q11, Q12, Q13, Q14, Q15, Q16, Q17, Q18, Q19, Q20, Q21, Q22, Q23, Q24, Q25, Q26, Q27, Q28, Q29, Q30, Q31, Q32, Q33, Q34, Q35, Q36, Q37, Q38, Q39, Q40, Q41, Q42, Q43, Q44, Q45, Q46, Q47, Q48, Q49, Q50, Q51, Q52, Q53, Q54, Q55, Q56, Q57, Q58, Q59, Q60, Q61]), "radius" : .5 * mm, "tangentPropagation" : true, "allowEdgeOverflow" : false});
        }
        {
            var Q0;
            Q0=makeQuery(id+"F1.opRevolve","SWEPT_EDGE",EDGE,{"disambiguationData":[OSD([sQuery(id+"F0.wireOp",EDGE,"E0"),sQuery(id+"F0.wireOp",EDGE,"E8")])]});
            var Q1;
            Q1=makeQuery(id+"F1.opRevolve","SWEPT_EDGE",EDGE,{"disambiguationData":[OSD([sQuery(id+"F0.wireOp",EDGE,"E7"),sQuery(id+"F0.wireOp",EDGE,"E8")])]});
            var Q2;
            Q2=makeQuery(id+"F1.opRevolve","SWEPT_EDGE",EDGE,{"disambiguationData":[OSD([sQuery(id+"F0.wireOp",EDGE,"E1"),sQuery(id+"F0.wireOp",EDGE,"E7")])]});
            var Q3;
            Q3=makeQuery(id+"F1.opRevolve","SWEPT_EDGE",EDGE,{"disambiguationData":[OSD([sQuery(id+"F0.wireOp",EDGE,"E3"),sQuery(id+"F0.wireOp",EDGE,"E4")])]});
            var Q4;
            Q4=makeQuery(id+"F1.opRevolve","SWEPT_EDGE",EDGE,{"disambiguationData":[OSD([sQuery(id+"F0.wireOp",EDGE,"E4"),sQuery(id+"F0.wireOp",EDGE,"E5")])]});
            fillet(context, id + "F14", {"entities" : qUnion([Q0, Q1, Q2, Q3, Q4]), "radius" : 1 * mm, "tangentPropagation" : true, "allowEdgeOverflow" : false});
        }
    });
